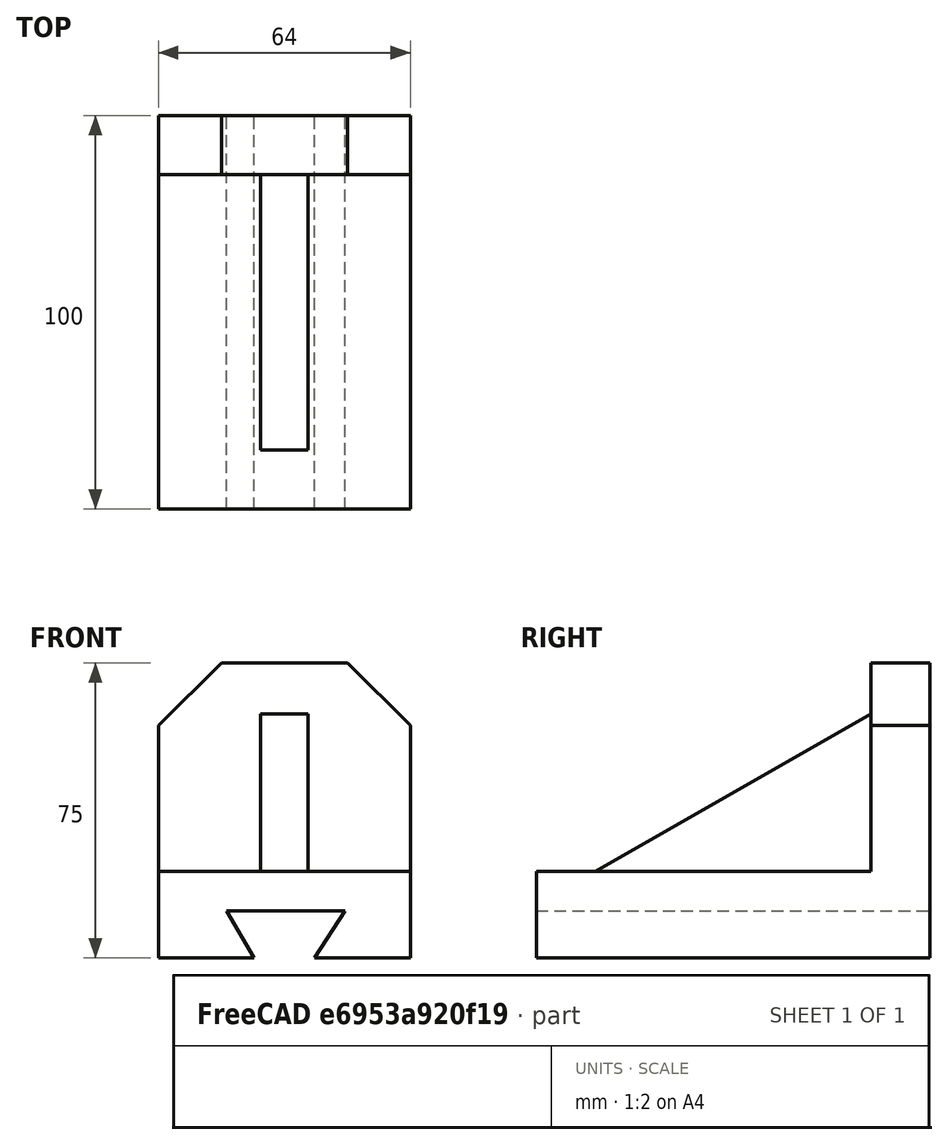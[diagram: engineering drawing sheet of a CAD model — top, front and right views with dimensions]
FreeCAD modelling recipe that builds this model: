
FCSTD DOCUMENT  (FreeCAD 0.18R4 (GitTag))
Label: ass 3 2nd sem
License: All rights reserved
LicenseURL: http://en.wikipedia.org/wiki/All_rights_reserved
objects: TechDraw::DrawViewDimension×13, Sketcher::SketchObject×5, TechDraw::DrawProjGroup×5, PartDesign::Pad×3, TechDraw::DrawViewAnnotation×3, TechDraw::DrawProjGroupItem×3, PartDesign::Pocket×2, PartDesign::Body×1, TechDraw::DrawSVGTemplate×1, TechDraw::DrawPage×1
note: 16 computed .brp shape members not serialized (recipe doc carries the construction recipe); baked Part::Feature solids carry a one-line shape summary decoded from their .brp

FEATURE [Sketcher::SketchObject] Sketch
  MapMode = 5
  Support = -> [XY_Plane]
  sketch-geometry (4):
    g0: LineSegment StartX=-32 StartY=50 StartZ=0 EndX=32 EndY=50 EndZ=0
    g1: LineSegment StartX=32 StartY=50 StartZ=0 EndX=32 EndY=-50 EndZ=0
    g2: LineSegment StartX=32 StartY=-50 StartZ=0 EndX=-32 EndY=-50 EndZ=0
    g3: LineSegment StartX=-32 StartY=-50 StartZ=0 EndX=-32 EndY=50 EndZ=0
  constraints (11):
    c: Coincident(g0,g1)
    c: Coincident(g1,g2)
    c: Coincident(g2,g3)
    c: Coincident(g3,g0)
    c: Horizontal(g0)
    c: Horizontal(g2)
    c: Vertical(g1)
    c: Vertical(g3)
    c: DistanceY(g3,g3) = 100
    c: DistanceX(g2,g2) = 64
    c: Symmetric(g0,g1,g-1)
FEATURE [PartDesign::Pad] Pad
  Length = 22
  Length2 = 100
  Profile = -> Sketch
  Type = 0
FEATURE [Sketcher::SketchObject] Sketch001
  MapMode = 5
  Placement = pos=(0,50,0) rot=(0,0.707107,0.707107;3.14159rad)
  Support = -> [Pad]
  sketch-geometry (6):
    g0: LineSegment StartX=-32 StartY=22 StartZ=0 EndX=-32 EndY=59 EndZ=0
    g1: LineSegment StartX=-32 StartY=59 StartZ=0 EndX=-16 EndY=75 EndZ=0
    g2: LineSegment StartX=-16 StartY=75 StartZ=0 EndX=16 EndY=75 EndZ=0
    g3: LineSegment StartX=16 StartY=75 StartZ=0 EndX=32 EndY=59 EndZ=0
    g4: LineSegment StartX=32 StartY=59 StartZ=0 EndX=32 EndY=22 EndZ=0
    g5: LineSegment StartX=32 StartY=22 StartZ=0 EndX=-32 EndY=22 EndZ=0
  constraints (16):
    c: Coincident(g0,g1)
    c: Coincident(g1,g2)
    c: Coincident(g2,g3)
    c: Coincident(g3,g4)
    c: Coincident(g4,g5)
    c: Coincident(g5,g0)
    c: DistanceX(g5,g5) = 64
    c: Symmetric(g0,g4,g-2)
    c: Parallel(g-2,g0)
    c: Parallel(g-2,g4)
    c: DistanceY(g0,g0) = 37
    c: DistanceY(g4,g4) = 37
    c: DistanceX(g2,g2) = 32
    c: Symmetric(g1,g2,g-2)
    c: DistanceY(g4,g2) = 53
    c: DistanceY(g-1,g4) = 22
FEATURE [PartDesign::Pad] Pad001
  BaseFeature = -> Pad
  Length = 15
  Length2 = 100
  Profile = -> Sketch001
  Reversed = true
  Type = 0
FEATURE [Sketcher::SketchObject] Sketch002
  MapMode = 5
  Placement = pos=(0,-50,0) rot=(1,0,0;1.5708rad)
  Support = -> [Pad001]
  sketch-geometry (4):
    g0: LineSegment StartX=-7.70709 StartY=0 StartZ=0 EndX=-14.6353 EndY=12 EndZ=0
    g1: LineSegment StartX=-14.6353 StartY=12 StartZ=0 EndX=15.3647 EndY=12 EndZ=0
    g2: LineSegment StartX=15.3647 StartY=12 StartZ=0 EndX=7.70709 EndY=0 EndZ=0
    g3: LineSegment StartX=7.70709 StartY=0 StartZ=0 EndX=-7.70709 EndY=0 EndZ=0
  constraints (10):
    c: Coincident(g0,g1)
    c: Coincident(g1,g2)
    c: Coincident(g2,g3)
    c: Coincident(g3,g0)
    c: Parallel(g3,g1)
    c: Symmetric(g2,g0,g-2)
    c: PointOnObject(g2,g-1)
    c: DistanceX(g1,g1) = 30
    c: Angle(g0,g3,g0) = 1.0472
    c: DistanceY(g-1,g1) = 12
FEATURE [PartDesign::Pocket] Pocket
  BaseFeature = -> Pad001
  Length = 5
  Length2 = 100
  Profile = -> Sketch002
  Type = 1
FEATURE [Sketcher::SketchObject] Sketch003
  ExternalGeometry = -> [Pocket]
  MapMode = 5
  Placement = pos=(0,0,22) rot=(0,0,1;0rad)
  Support = -> [Pocket]
  sketch-geometry (4):
    g0: LineSegment StartX=-6 StartY=35 StartZ=0 EndX=6 EndY=35 EndZ=0
    g1: LineSegment StartX=6 StartY=35 StartZ=0 EndX=6 EndY=-35 EndZ=0
    g2: LineSegment StartX=6 StartY=-35 StartZ=0 EndX=-6 EndY=-35 EndZ=0
    g3: LineSegment StartX=-6 StartY=-35 StartZ=0 EndX=-6 EndY=35 EndZ=0
  constraints (11):
    c: Coincident(g0,g1)
    c: Coincident(g1,g2)
    c: Coincident(g2,g3)
    c: Coincident(g3,g0)
    c: Horizontal(g2)
    c: Vertical(g1)
    c: Vertical(g3)
    c: DistanceY(g1,g1) = 70
    c: DistanceX(g0,g0) = 12
    c: Symmetric(g0,g0,g-2)
    c: PointOnObject(g0,g-4)
FEATURE [PartDesign::Pad] Pad002
  BaseFeature = -> Pocket
  Length = 40
  Length2 = 100
  Profile = -> Sketch003
  Type = 0
FEATURE [Sketcher::SketchObject] Sketch004
  ExternalGeometry = -> [Pad002]
  MapMode = 5
  Placement = pos=(-6,0,0) rot=(0.57735,-0.57735,-0.57735;2.0944rad)
  Support = -> [Pad002]
  sketch-geometry (3):
    g0: LineSegment StartX=-35 StartY=62 StartZ=0 EndX=35 EndY=22 EndZ=0
    g1: LineSegment StartX=35 StartY=22 StartZ=0 EndX=35 EndY=62 EndZ=0
    g2: LineSegment StartX=35 StartY=62 StartZ=0 EndX=-35 EndY=62 EndZ=0
  constraints (6):
    c: Coincident(g0,g1)
    c: Coincident(g1,g2)
    c: Coincident(g2,g0)
    c: Coincident(g2,g-4)
    c: Coincident(g1,g-4)
    c: Coincident(g-3,g0)
FEATURE [PartDesign::Pocket] Pocket001
  BaseFeature = -> Pad002
  Length = 12
  Length2 = 100
  Profile = -> Sketch004
  Type = 0
FEATURE [PartDesign::Body] Body
  Group = -> [Sketch,Pad,Sketch001,Pad001,Sketch002,Pocket,Sketch003,Pad002,Sketch004,Pocket001]
  Origin = -> Origin
  Tip = -> Pocket001
FEATURE [TechDraw::DrawSVGTemplate] Template
  EditableTexts = Designed_by_Name=Soumojit Shome; Drawing_number=Drawing number; FC-Date=Date; FC-SC=1:1; FC-SH=Sheet; FC-Title=Title; Subtitle=ECE2(Y) 16900322101; Weight=Weight
  Height = 210
  Orientation = 1
  Width = 297
FEATURE [TechDraw::DrawProjGroup] ProjGroup
  AutoDistribute = true
  LockPosition = false
  ProjectionType = 0
  Rotation = 0
  ScaleType = 0
  Source = -> [Pocket001]
  X = -12.7788
  Y = 170.302
  spacingX = 15
  spacingY = 15
FEATURE [TechDraw::DrawViewAnnotation] Annotation
  Font = osifont
  LineSpace = 80
  LockPosition = false
  MaxWidth = -1
  Rotation = 0
  ScaleType = 0
  Text = Front View
  TextSize = 6
  TextStyle = 0
  X = 89.2963
  Y = 109.872
FEATURE [TechDraw::DrawProjGroupItem] ProjItem001  label="Front001"
  CoarseView = false
  Direction = (0,0,1)
  Focus = 100
  HardHidden = false
  IsoCount = 0
  IsoHidden = false
  IsoVisible = false
  LockPosition = true
  Perspective = false
  Rotation = 0
  RotationVector = (0,-1,0)
  ScaleType = 2
  SeamHidden = false
  SeamVisible = false
  SmoothHidden = false
  SmoothVisible = false
  Source = -> [Pocket001]
  Type = 0
  X = 0
  Y = 0
FEATURE [TechDraw::DrawProjGroup] ProjGroup001
  Anchor = -> ProjItem001
  AutoDistribute = true
  LockPosition = false
  ProjectionType = 0
  Rotation = 0
  ScaleType = 0
  Source = -> [Pocket001]
  Views = -> [ProjItem001]
  X = 75.4565
  Y = 65.1581
  spacingX = 15
  spacingY = 15
FEATURE [TechDraw::DrawProjGroup] ProjGroup002
  AutoDistribute = true
  LockPosition = false
  ProjectionType = 0
  Rotation = 0
  ScaleType = 0
  Source = -> [Pocket001]
  X = 220.298
  Y = 127.411
  spacingX = 15
  spacingY = 15
FEATURE [TechDraw::DrawProjGroupItem] ProjItem002  label="Front002"
  CoarseView = false
  Direction = (-0.489,-0.739,0.463)
  Focus = 100
  HardHidden = false
  IsoCount = 0
  IsoHidden = false
  IsoVisible = false
  LockPosition = true
  Perspective = false
  Rotation = 0
  RotationVector = (0.837,-0.547,0.011)
  ScaleType = 2
  SeamHidden = false
  SeamVisible = false
  SmoothHidden = false
  SmoothVisible = false
  Source = -> [Pocket001]
  Type = 0
  X = 0
  Y = 0
FEATURE [TechDraw::DrawProjGroup] ProjGroup003
  Anchor = -> ProjItem002
  AutoDistribute = true
  LockPosition = false
  ProjectionType = 0
  Rotation = 0
  ScaleType = 0
  Source = -> [Pocket001]
  Views = -> [ProjItem002]
  X = 223.204
  Y = 124.091
  spacingX = 15
  spacingY = 15
FEATURE [TechDraw::DrawViewAnnotation] Annotation001
  Font = osifont
  LineSpace = 80
  LockPosition = false
  MaxWidth = -1
  Rotation = 0
  ScaleType = 0
  Text = Isometric View
  TextSize = 6
  TextStyle = 0
  X = 222.789
  Y = 72.6285
FEATURE [TechDraw::DrawViewAnnotation] Annotation002
  Font = osifont
  LineSpace = 80
  LockPosition = false
  MaxWidth = -1
  Rotation = 0
  ScaleType = 0
  Text = Top View
  TextSize = 6
  TextStyle = 0
  X = 78.7767
  Y = 22.4111
FEATURE [TechDraw::DrawViewDimension] Dimension
  Arbitrary = false
  FormatSpec = %.2f
  LockPosition = false
  MeasureType = 1
  OverTolerance = 0
  References2D = -> [ProjItem001]
  Rotation = 0
  ScaleType = 0
  Type = 1
  UnderTolerance = 0
  X = -43.33
  Y = 40.3004
FEATURE [TechDraw::DrawViewDimension] Dimension001
  Arbitrary = false
  FormatSpec = %.2f
  LockPosition = false
  MeasureType = 1
  OverTolerance = 0
  References2D = -> [ProjItem001]
  Rotation = 0
  ScaleType = 0
  Type = 2
  UnderTolerance = 0
  X = -57.0553
  Y = -22.7549
FEATURE [TechDraw::DrawViewDimension] Dimension005
  Arbitrary = false
  FormatSpec = %.2f
  LockPosition = false
  MeasureType = 1
  OverTolerance = 0
  References2D = -> [ProjItem001]
  Rotation = 0
  ScaleType = 0
  Type = 2
  UnderTolerance = 0
  X = 35.8661
  Y = 17.3223
FEATURE [TechDraw::DrawProjGroupItem] ProjItem003  label="Front003"
  CoarseView = false
  Direction = (0,-1,0)
  Focus = 100
  HardHidden = false
  IsoCount = 0
  IsoHidden = false
  IsoVisible = false
  LockPosition = true
  Perspective = false
  Rotation = 0
  RotationVector = (1,0,0)
  ScaleType = 2
  SeamHidden = false
  SeamVisible = false
  SmoothHidden = false
  SmoothVisible = false
  Source = -> [Pocket001]
  Type = 0
  X = 0
  Y = 0
FEATURE [TechDraw::DrawProjGroup] ProjGroup004
  Anchor = -> ProjItem003
  AutoDistribute = true
  LockPosition = false
  ProjectionType = 0
  Rotation = 0
  ScaleType = 0
  Source = -> [Pocket001]
  Views = -> [ProjItem003]
  X = 87.4391
  Y = 158.699
  spacingX = 15
  spacingY = 15
FEATURE [TechDraw::DrawViewDimension] Dimension008
  Arbitrary = false
  FormatSpec = %.2f
  LockPosition = false
  MeasureType = 1
  OverTolerance = 0
  References2D = -> [ProjItem003]
  Rotation = 0
  ScaleType = 0
  Type = 2
  UnderTolerance = 0
  X = 14.2281
  Y = 4.5
FEATURE [TechDraw::DrawViewDimension] Dimension009
  Arbitrary = false
  FormatSpec = %.2f
  LockPosition = false
  MeasureType = 1
  OverTolerance = 0
  References2D = -> [ProjItem001]
  Rotation = 0
  ScaleType = 0
  Type = 1
  UnderTolerance = 0
  X = 1.29917
  Y = -13.362
FEATURE [TechDraw::DrawViewDimension] Dimension010
  Arbitrary = false
  FormatSpec = %.2f
  LockPosition = false
  MeasureType = 1
  OverTolerance = 0
  References2D = -> [ProjItem001]
  Rotation = 0
  ScaleType = 0
  Type = 1
  UnderTolerance = 0
  X = 0
  Y = -35.4645
FEATURE [TechDraw::DrawViewDimension] Dimension011
  Arbitrary = false
  FormatSpec = %.2f
  LockPosition = false
  MeasureType = 1
  OverTolerance = 0
  References2D = -> [ProjItem003]
  Rotation = 0
  ScaleType = 0
  Type = 2
  UnderTolerance = 0
  X = 44.7867
  Y = -3.46445
FEATURE [TechDraw::DrawViewDimension] Dimension012
  Arbitrary = false
  FormatSpec = %.2f
  LockPosition = false
  MeasureType = 1
  OverTolerance = 0
  References2D = -> [ProjItem003]
  Rotation = 0
  ScaleType = 0
  Type = 2
  UnderTolerance = 0
  X = -46.5189
  Y = 29.0669
FEATURE [TechDraw::DrawViewDimension] Dimension013
  Arbitrary = false
  FormatSpec = %.2f
  LockPosition = false
  MeasureType = 1
  OverTolerance = 0
  References2D = -> [ProjItem003]
  Rotation = 0
  ScaleType = 0
  Type = 1
  UnderTolerance = 0
  X = -0.501408
  Y = -19.4372
FEATURE [TechDraw::DrawViewDimension] Dimension014
  Arbitrary = false
  FormatSpec = %.2f
  LockPosition = false
  MeasureType = 1
  OverTolerance = 0
  References2D = -> [ProjItem003]
  Rotation = 0
  ScaleType = 0
  Type = 1
  UnderTolerance = 0
  X = 19.0545
  Y = -40.9644
FEATURE [TechDraw::DrawViewDimension] Dimension015
  Arbitrary = false
  FormatSpec = %.2f
  LockPosition = false
  MeasureType = 1
  OverTolerance = 0
  References2D = -> [ProjItem003]
  Rotation = 0
  ScaleType = 0
  Type = 2
  UnderTolerance = 0
  X = -49.7132
  Y = -26.7364
FEATURE [TechDraw::DrawViewDimension] Dimension016
  Arbitrary = false
  FormatSpec = %.2f
  LockPosition = false
  MeasureType = 1
  OverTolerance = 0
  References2D = -> [ProjItem003]
  Rotation = 0
  ScaleType = 0
  Type = 2
  UnderTolerance = 0
  X = -64.4792
  Y = -23.0355
FEATURE [TechDraw::DrawViewDimension] Dimension017
  Arbitrary = false
  FormatSpec = %.2f
  LockPosition = false
  MeasureType = 1
  OverTolerance = 0
  References2D = -> [ProjItem003]
  Rotation = 0
  ScaleType = 0
  Type = 6
  UnderTolerance = 0
  X = -19.9826
  Y = -29.2529
FEATURE [TechDraw::DrawPage] Page
  KeepUpdated = true
  ProjectionType = 0
  Template = -> Template
  Views = -> [ProjGroup,Annotation,ProjGroup001,ProjGroup002,ProjGroup003,Annotation001,Annotation002,Dimension,Dimension001,Dimension005,ProjGroup004,Dimension008,Dimension009,Dimension010,Dimension011,Dimension012,Dimension013,Dimension014,Dimension015,Dimension016,Dimension017]
